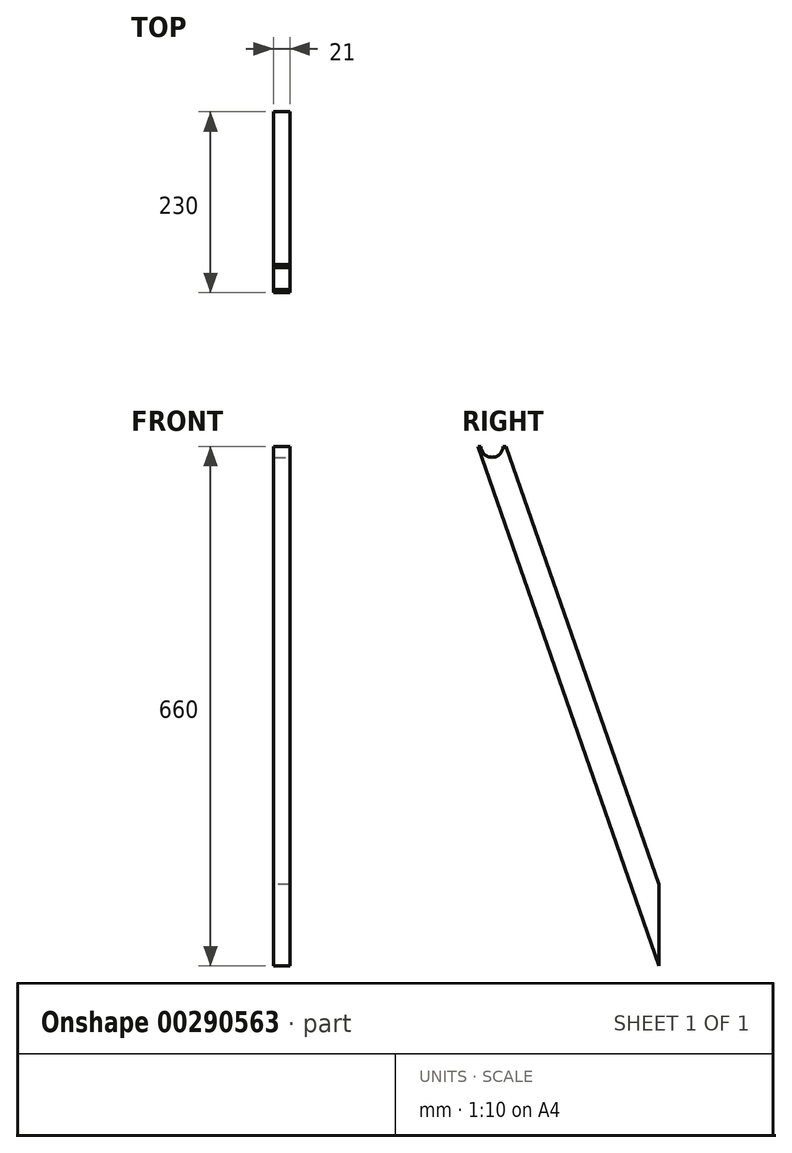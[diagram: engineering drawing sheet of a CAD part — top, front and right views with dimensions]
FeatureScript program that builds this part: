
annotation { "Feature Type Name" : "Feature", "Feature Type Description" : "" }
export const myFeature = defineFeature(function(context is Context, id is Id, definition is map)
    precondition{}
    {
        {
            var Q0;
            Q0=qCreatedBy(makeId("Right.planeOp"),FACE);
            var sketch = newSketch(context, id + "F0", { "sketchPlane" : qUnion([Q0])});
            skLineSegment(sketch, "E0", {"start": v(0, 0) * mm, "end": v(0, 660) * mm, "construction": true});
            skLineSegment(sketch, "E1", {"start": v(0, 660) * mm, "end": v(-230, 660) * mm, "construction": true});
            skLineSegment(sketch, "E2", {"start": v(-230, 660) * mm, "end": v(0, 0) * mm});
            skLineSegment(sketch, "E3", {"start": v(0, 103.32) * mm, "end": v(-194, 660) * mm});
            skLineSegment(sketch, "E4", {"start": v(-194, 660) * mm, "end": v(-230, 660) * mm});
            skLineSegment(sketch, "E5", {"start": v(0, 0) * mm, "end": v(0, 103.32) * mm});
            skSolve(sketch);
        }
        {
            var Q0;
            Q0 = qSketchRegion(id + "F0", true);
            extrude(context, id + "F1", {"entities" : qUnion([Q0]), "depth" : 21 * mm});
        }
        {
            var Q0;
            Q0=makeQuery(id+"F1.opExtrude","CAP_FACE",FACE,{"disambiguationData":[OSD([sQuery(id+"F0.wireOp",EDGE,"E2"),sQuery(id+"F0.wireOp",EDGE,"E3"),sQuery(id+"F0.wireOp",EDGE,"E4"),sQuery(id+"F0.wireOp",EDGE,"E5")])],"isStart":false});
            var sketch = newSketch(context, id + "F2", { "sketchPlane" : qUnion([Q0])});
            skCircle(sketch, "E6", {"center": v(-212, 660) * mm, "radius": 14 * mm});
            skSolve(sketch);
        }
        {
            var Q0;
            Q0 = qSketchRegion(id + "F2", true);
            extrude(context, id + "F3", {"entities" : qUnion([Q0]), "operationType" : NewBodyOperationType.REMOVE, "oppositeDirection" : true, "depth" : 25 * mm});
        }
    });
